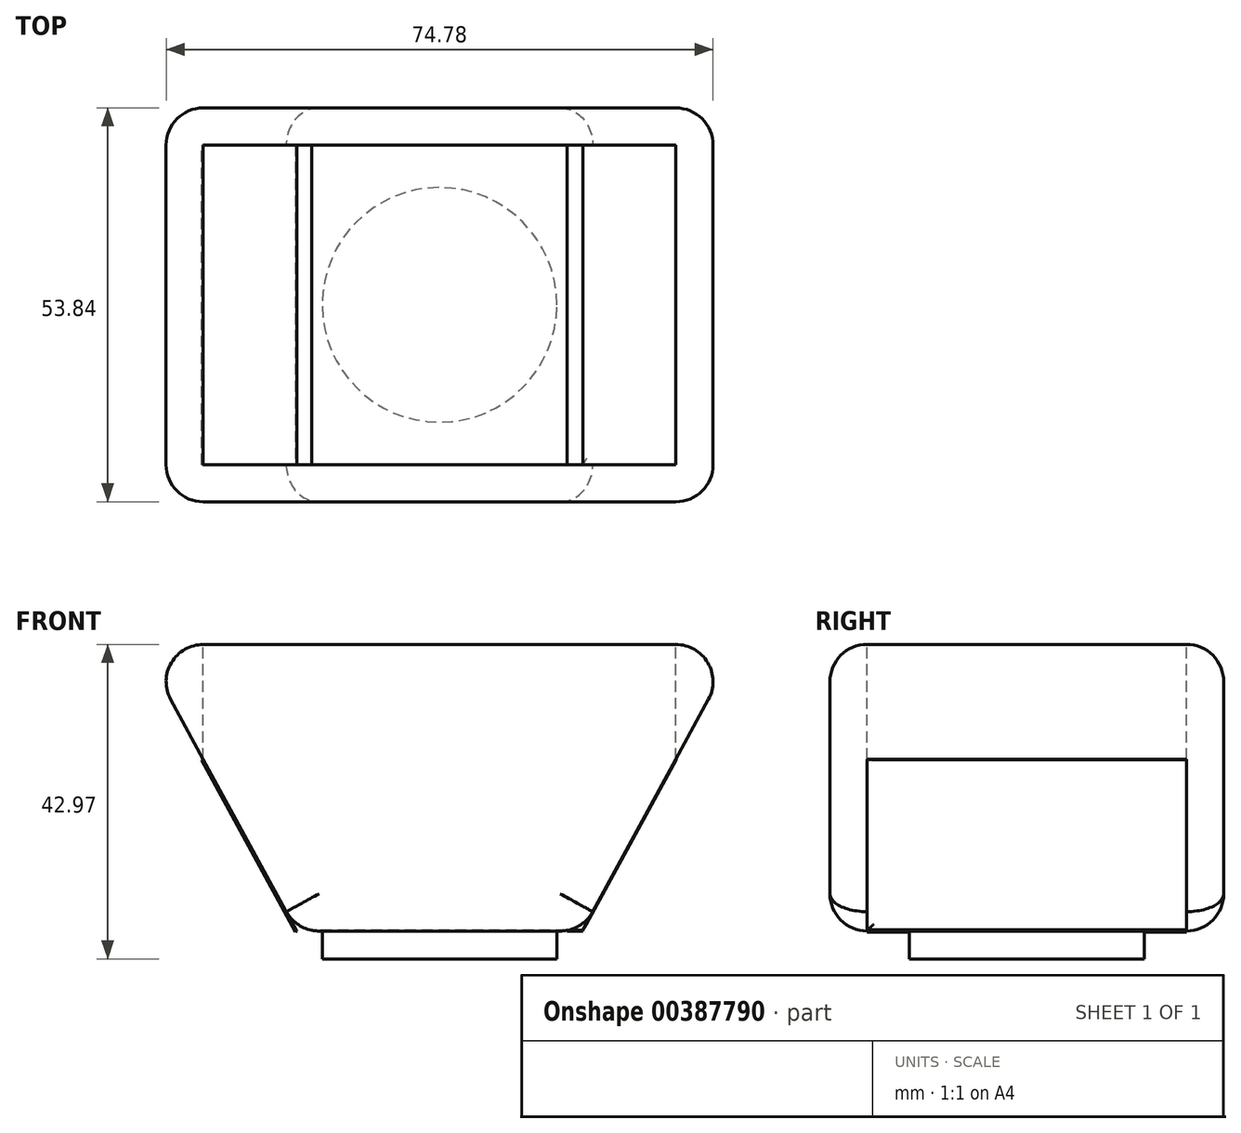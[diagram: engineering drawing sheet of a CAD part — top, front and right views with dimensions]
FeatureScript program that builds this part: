
annotation { "Feature Type Name" : "Feature", "Feature Type Description" : "" }
export const myFeature = defineFeature(function(context is Context, id is Id, definition is map)
    precondition{}
    {
        {
            var Q0;
            Q0=qCreatedBy(makeId("Top.planeOp"),FACE);
            var sketch = newSketch(context, id + "F0", { "sketchPlane" : qUnion([Q0])});
            skCircle(sketch, "E0", {"center": v(0, 0) * mm, "radius": 16.04 * mm});
            skSolve(sketch);
        }
        {
            var Q0;
            Q0=makeQuery(id+"F0.imprint","IMPRINT",FACE,{"disambiguationData":[TD([[makeQuery(id+"F0.imprint","IMPRINT",EDGE,{"derivedFrom":sQuery(id+"F0.wireOp",EDGE,"E0")}),1.0]])]});
            extrude(context, id + "F1", {"entities" : qUnion([Q0]), "oppositeDirection" : true, "depth" : 3.8 * mm});
        }
        {
            var Q0;
            Q0=qCreatedBy(makeId("Front.planeOp"),FACE);
            var sketch = newSketch(context, id + "F2", { "sketchPlane" : qUnion([Q0])});
            skLineSegment(sketch, "E1", {"start": v(-19.5, 0) * mm, "end": v(-40.87, 39.16) * mm});
            skLineSegment(sketch, "E2.MirrorCS", {"start": v(19.5, 0) * mm, "end": v(40.87, 39.16) * mm});
            skLineSegment(sketch, "E3", {"start": v(-41.78, 45.13) * mm, "end": v(0, 45.13) * mm});
            skLineSegment(sketch, "E4.MirrorCS", {"start": v(41.78, 45.13) * mm, "end": v(0, 45.13) * mm});
            skLineSegment(sketch, "E5", {"start": v(-40.87, 39.16) * mm, "end": v(-40.87, 39.62) * mm});
            skLineSegment(sketch, "E6", {"start": v(-40.87, 39.62) * mm, "end": v(-41.78, 39.62) * mm});
            skLineSegment(sketch, "E7", {"start": v(-41.78, 45.13) * mm, "end": v(-41.78, 39.62) * mm});
            skLineSegment(sketch, "E8", {"start": v(40.87, 39.62) * mm, "end": v(40.87, 39.16) * mm});
            skLineSegment(sketch, "E9.MirrorCS", {"start": v(41.78, 45.13) * mm, "end": v(41.78, 39.62) * mm});
            skLineSegment(sketch, "E10.MirrorCS", {"start": v(40.87, 39.62) * mm, "end": v(41.78, 39.62) * mm});
            skLineSegment(sketch, "E11", {"start": v(40.87, 39.16) * mm, "end": v(-40.87, 39.16) * mm});
            skLineSegment(sketch, "E12", {"start": v(-40.87, 39.62) * mm, "end": v(40.87, 39.62) * mm});
            skLineSegment(sketch, "E13", {"start": v(-19.5, 0) * mm, "end": v(19.5, 0) * mm});
            skSolve(sketch);
        }
        {
            var Q0;
            Q0=makeQuery(id+"F2.imprint","IMPRINT",FACE,{"disambiguationData":[TD([[makeQuery(id+"F2.imprint","IMPRINT",EDGE,{"derivedFrom":sQuery(id+"F2.wireOp",EDGE,"E1")}),-1.0]])]});
            extrude(context, id + "F3", {"entities" : qUnion([Q0]), "operationType" : NewBodyOperationType.ADD, "endBound" : BoundingType.SYMMETRIC, "depth" : 53.85 * mm});
        }
        {
            var Q0;
            {var subQ0=sQuery(id+"F2.wireOp",EDGE,"E13");var subQ1=sQuery(id+"F2.wireOp",EDGE,"E1");Q0=makeQuery(id+"F3.boolean.opBoolean","SPLIT",EDGE,{"disambiguationData":[TD([makeQuery(id+"F3.opExtrude","CAP_FACE",FACE,{"disambiguationData":[OSD([subQ1,sQuery(id+"F2.wireOp",EDGE,"E2.MirrorCS"),sQuery(id+"F2.wireOp",EDGE,"E11"),subQ0])],"isStart":false})])],"derivedFrom":makeQuery(id+"F3.opExtrude","SWEPT_EDGE",EDGE,{"disambiguationData":[OSD([subQ1,subQ0])]})});}
            var Q1;
            Q1=makeQuery(id+"F3.opExtrude","CAP_EDGE",EDGE,{"disambiguationData":[OSD([sQuery(id+"F2.wireOp",EDGE,"E13")])],"isStart":false});
            var Q2;
            {var subQ0=sQuery(id+"F2.wireOp",EDGE,"E13");var subQ1=sQuery(id+"F2.wireOp",EDGE,"E2.MirrorCS");Q2=makeQuery(id+"F3.boolean.opBoolean","SPLIT",EDGE,{"disambiguationData":[TD([makeQuery(id+"F3.opExtrude","CAP_FACE",FACE,{"disambiguationData":[OSD([sQuery(id+"F2.wireOp",EDGE,"E1"),subQ1,sQuery(id+"F2.wireOp",EDGE,"E11"),subQ0])],"isStart":false})])],"derivedFrom":makeQuery(id+"F3.opExtrude","SWEPT_EDGE",EDGE,{"disambiguationData":[OSD([subQ1,subQ0])]})});}
            var Q3;
            {var subQ0=sQuery(id+"F2.wireOp",EDGE,"E13");var subQ1=sQuery(id+"F2.wireOp",EDGE,"E2.MirrorCS");Q3=makeQuery(id+"F3.boolean.opBoolean","SPLIT",EDGE,{"disambiguationData":[TD([makeQuery(id+"F3.opExtrude","CAP_FACE",FACE,{"disambiguationData":[OSD([sQuery(id+"F2.wireOp",EDGE,"E1"),subQ1,sQuery(id+"F2.wireOp",EDGE,"E11"),subQ0])],"isStart":true})])],"derivedFrom":makeQuery(id+"F3.opExtrude","SWEPT_EDGE",EDGE,{"disambiguationData":[OSD([subQ1,subQ0])]})});}
            var Q4;
            Q4=makeQuery(id+"F3.opExtrude","CAP_EDGE",EDGE,{"disambiguationData":[OSD([sQuery(id+"F2.wireOp",EDGE,"E13")])],"isStart":true});
            var Q5;
            {var subQ0=sQuery(id+"F2.wireOp",EDGE,"E1");var subQ1=sQuery(id+"F2.wireOp",EDGE,"E13");Q5=makeQuery(id+"F3.boolean.opBoolean","SPLIT",EDGE,{"disambiguationData":[TD([makeQuery(id+"F3.opExtrude","CAP_FACE",FACE,{"disambiguationData":[OSD([subQ0,sQuery(id+"F2.wireOp",EDGE,"E2.MirrorCS"),sQuery(id+"F2.wireOp",EDGE,"E11"),subQ1])],"isStart":true})])],"derivedFrom":makeQuery(id+"F3.opExtrude","SWEPT_EDGE",EDGE,{"disambiguationData":[OSD([subQ0,subQ1])]})});}
            fillet(context, id + "F4", {"entities" : qUnion([Q0, Q1, Q2, Q3, Q4, Q5]), "radius" : 5.08 * mm, "tangentPropagation" : true, "allowEdgeOverflow" : false});
        }
        {
            var Q0;
            Q0=makeQuery(id+"F3.opExtrude","CAP_EDGE",EDGE,{"disambiguationData":[OSD([sQuery(id+"F2.wireOp",EDGE,"E1")])],"isStart":false});
            var Q1;
            Q1=makeQuery(id+"F3.opExtrude","CAP_EDGE",EDGE,{"disambiguationData":[OSD([sQuery(id+"F2.wireOp",EDGE,"E2.MirrorCS")])],"isStart":false});
            var Q2;
            Q2=makeQuery(id+"F3.opExtrude","SWEPT_EDGE",EDGE,{"disambiguationData":[OSD([sQuery(id+"F2.wireOp",EDGE,"E1"),sQuery(id+"F2.wireOp",EDGE,"E5"),sQuery(id+"F2.wireOp",EDGE,"E11")])]});
            var Q3;
            Q3=makeQuery(id+"F3.opExtrude","CAP_EDGE",EDGE,{"disambiguationData":[OSD([sQuery(id+"F2.wireOp",EDGE,"E11")])],"isStart":false});
            var Q4;
            Q4=makeQuery(id+"F3.opExtrude","CAP_EDGE",EDGE,{"disambiguationData":[OSD([sQuery(id+"F2.wireOp",EDGE,"E1")])],"isStart":true});
            var Q5;
            Q5=makeQuery(id+"F3.opExtrude","CAP_EDGE",EDGE,{"disambiguationData":[OSD([sQuery(id+"F2.wireOp",EDGE,"E11")])],"isStart":true});
            var Q6;
            Q6=makeQuery(id+"F3.opExtrude","SWEPT_EDGE",EDGE,{"disambiguationData":[OSD([sQuery(id+"F2.wireOp",EDGE,"E2.MirrorCS"),sQuery(id+"F2.wireOp",EDGE,"E8"),sQuery(id+"F2.wireOp",EDGE,"E11")])]});
            var Q7;
            Q7=makeQuery(id+"F3.opExtrude","CAP_EDGE",EDGE,{"disambiguationData":[OSD([sQuery(id+"F2.wireOp",EDGE,"E2.MirrorCS")])],"isStart":true});
            fillet(context, id + "F5", {"entities" : qUnion([Q0, Q1, Q2, Q3, Q4, Q5, Q6, Q7]), "radius" : 5.08 * mm, "tangentPropagation" : true, "allowEdgeOverflow" : false});
        }
        {
            var Q0;
            Q0=makeQuery(id+"F3.opExtrude","SWEPT_FACE",FACE,{"disambiguationData":[OSD([sQuery(id+"F2.wireOp",EDGE,"E11")])]});
            var Q1;
            Q1=sQuery(id+"F0.wireOp",EDGE,"E0");
            extrude(context, id + "F6", {"entities" : qUnion([Q0]), "operationType" : NewBodyOperationType.REMOVE, "surfaceEntities" : qUnion([Q1]), "oppositeDirection" : true, "depth" : 39.07 * mm});
        }
        {
            var Q0;
            Q0=makeQuery(id+"F3.opExtrude","SWEPT_FACE",FACE,{"disambiguationData":[OSD([sQuery(id+"F2.wireOp",EDGE,"E2.MirrorCS")])]});
            var sketch = newSketch(context, id + "F7", { "sketchPlane" : qUnion([Q0])});
            skLineSegment(sketch, "E14", {"start": v(-21.84, 36.08) * mm, "end": v(-21.84, 9.5) * mm});
            skLineSegment(sketch, "E15", {"start": v(-21.84, 9.5) * mm, "end": v(21.84, 9.5) * mm});
            skLineSegment(sketch, "E16", {"start": v(21.84, 9.5) * mm, "end": v(21.84, 36.08) * mm});
            skLineSegment(sketch, "E17", {"start": v(21.84, 36.08) * mm, "end": v(-21.84, 36.08) * mm});
            skSolve(sketch);
        }
        {
            var Q0;
            Q0 = qSketchRegion(id + "F7", true);
            extrude(context, id + "F8", {"entities" : qUnion([Q0]), "depth" : 0.08 * mm});
        }
        {
            var Q0;
            Q0=makeQuery(id+"F3.opExtrude","SWEPT_FACE",FACE,{"disambiguationData":[OSD([sQuery(id+"F2.wireOp",EDGE,"E13")])]});
            var sketch = newSketch(context, id + "F9", { "sketchPlane" : qUnion([Q0])});
            skLineSegment(sketch, "E18", {"start": v(17.45, 21.84) * mm, "end": v(19.57, 21.84) * mm});
            skLineSegment(sketch, "E19", {"start": v(19.57, 21.84) * mm, "end": v(19.57, -21.84) * mm});
            skLineSegment(sketch, "E20", {"start": v(19.57, -21.84) * mm, "end": v(17.45, -21.84) * mm});
            skLineSegment(sketch, "E21", {"start": v(17.45, -21.84) * mm, "end": v(17.45, 21.84) * mm});
            skSolve(sketch);
        }
        {
            var Q0;
            Q0 = qSketchRegion(id + "F9", true);
            extrude(context, id + "F10", {"entities" : qUnion([Q0]), "operationType" : NewBodyOperationType.ADD, "oppositeDirection" : true, "depth" : 0.13 * mm});
        }
        {
            var Q0;
            Q0=makeQuery(id+"F3.opExtrude","SWEPT_FACE",FACE,{"disambiguationData":[OSD([sQuery(id+"F2.wireOp",EDGE,"E1")])]});
            var sketch = newSketch(context, id + "F11", { "sketchPlane" : qUnion([Q0])});
            skLineSegment(sketch, "E22", {"start": v(-21.84, 36.08) * mm, "end": v(-21.84, 9.34) * mm});
            skLineSegment(sketch, "E23", {"start": v(-21.84, 9.34) * mm, "end": v(21.87, 9.34) * mm});
            skLineSegment(sketch, "E24", {"start": v(21.87, 9.34) * mm, "end": v(21.84, 36.08) * mm});
            skLineSegment(sketch, "E25", {"start": v(21.84, 36.08) * mm, "end": v(-21.84, 36.08) * mm});
            skSolve(sketch);
        }
        {
            var Q0;
            Q0 = qSketchRegion(id + "F11", true);
            extrude(context, id + "F12", {"entities" : qUnion([Q0]), "depth" : 0.25 * mm});
        }
        {
            var Q0;
            Q0=makeQuery(id+"F10.opExtrude","CAP_EDGE",EDGE,{"disambiguationData":[OSD([sQuery(id+"F9.wireOp",EDGE,"E20")])],"isStart":true});
            var Q1;
            Q1=makeQuery(id+"F8.opExtrude","CAP_EDGE",EDGE,{"disambiguationData":[OSD([sQuery(id+"F7.wireOp",EDGE,"E15")])],"isStart":false});
            var Q2;
            Q2=makeQuery(id+"F8.opExtrude","CAP_EDGE",EDGE,{"disambiguationData":[OSD([sQuery(id+"F7.wireOp",EDGE,"E14")])],"isStart":false});
            fillet(context, id + "F13", {"entities" : qUnion([Q0, Q1, Q2]), "radius" : 5.08 * mm, "tangentPropagation" : true, "allowEdgeOverflow" : false});
        }
    });
